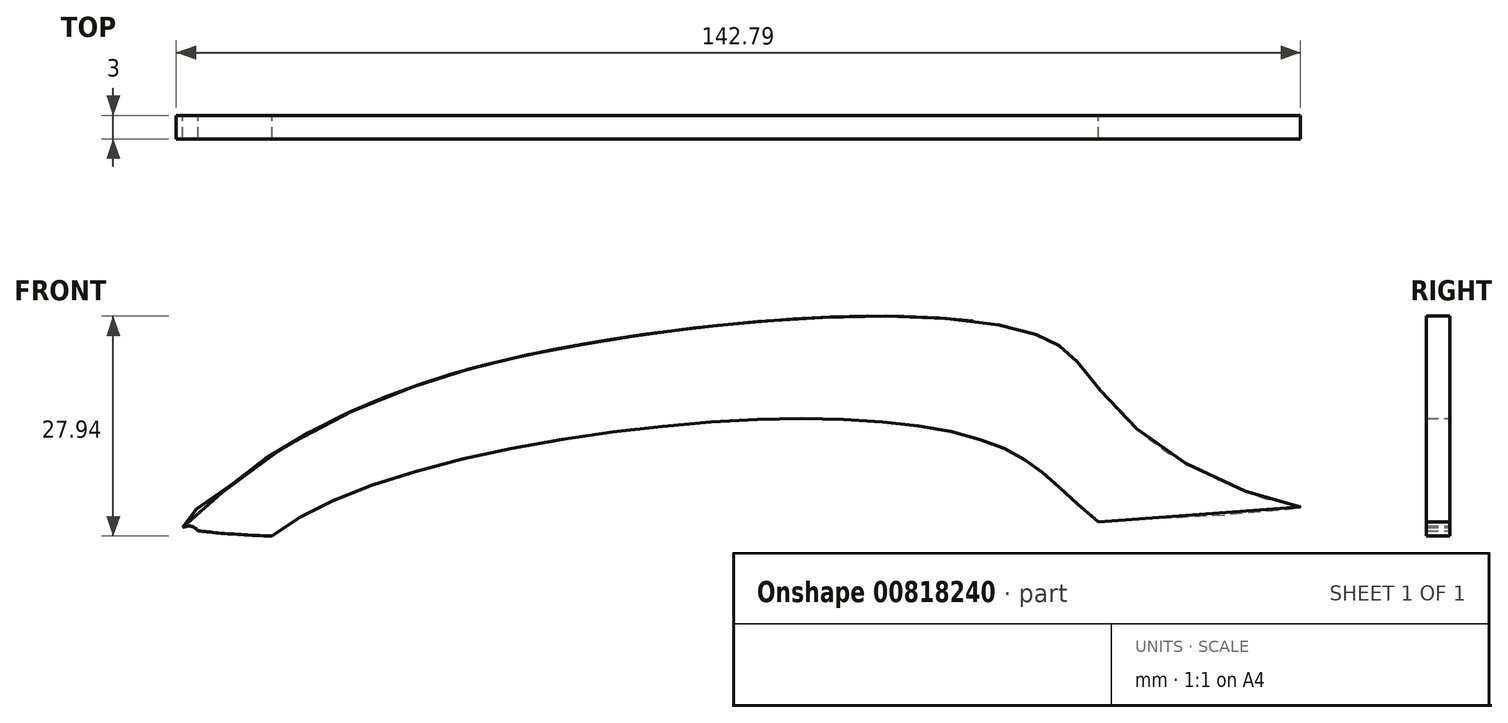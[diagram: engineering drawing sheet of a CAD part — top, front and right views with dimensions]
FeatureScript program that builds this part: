
annotation { "Feature Type Name" : "Feature", "Feature Type Description" : "" }
export const myFeature = defineFeature(function(context is Context, id is Id, definition is map)
    precondition{}
    {
        {
            var Q0;
            Q0=qCreatedBy(makeId("Front.planeOp"),FACE);
            var sketch = newSketch(context, id + "F0", { "sketchPlane" : qUnion([Q0])});
            skCircle(sketch, "E0", {"center": v(-68.28, 0) * mm, "radius": 1.5 * mm});
            skCircle(sketch, "E1", {"center": v(71.72, 0) * mm, "radius": 1.5 * mm});
            skArc(sketch, "E2", {"start": v(-73.43, 6.13) * mm, "mid": v(-73.34, -6.2) * mm, "end": v(-61.25, -3.82) * mm});
            skArc(sketch, "E3", {"start": v(67.99, -9.28) * mm, "mid": v(81.18, -3.23) * mm, "end": v(74.44, 9.62) * mm});
            skFitSpline(sketch, "E4", {"points": [v(-73.43, 6.13) * mm, v(-19, 30.54) * mm, v(44.44, 30.12) * mm, v(74.44, 9.62) * mm], "startDerivative": vector(148.64, 124.78) * mm, "endDerivative": vector(251.37, -71.25) * mm});
            skFitSpline(sketch, "E5", {"points": [v(-61.25, -3.82) * mm, v(-8.1, 14.18) * mm, v(36.46, 10.8) * mm, v(67.99, -9.28) * mm], "startDerivative": vector(43.16, 79.54) * mm, "endDerivative": vector(229.82, -92.38) * mm});
            skFitSpline(sketch, "E6.0", {"points": [v(-69.57, 1.53) * mm, v(-66.6, 4.03) * mm, v(-60.85, 8.45) * mm, v(-52.52, 13.63) * mm, v(-45.53, 17) * mm, v(-39.7, 19.23) * mm, v(-35.17, 20.71) * mm, v(-30.42, 22.03) * mm, v(-25.43, 23.2) * mm, v(-21.01, 24.09) * mm, v(-17.31, 24.75) * mm, v(-13.5, 25.38) * mm, v(-8.6, 26.1) * mm, v(-2.53, 26.85) * mm, v(3.58, 27.45) * mm, v(9.65, 27.88) * mm, v(15.57, 28.12) * mm, v(21.24, 28.15) * mm, v(26.55, 27.96) * mm, v(31.37, 27.53) * mm, v(34.89, 26.98) * mm, v(37.31, 26.42) * mm, v(38.92, 25.96) * mm, v(40.3, 25.46) * mm, v(41.22, 25.04) * mm, v(41.82, 24.71) * mm, v(42.37, 24.37) * mm, v(42.99, 23.93) * mm, v(43.69, 23.3) * mm, v(44.41, 22.57) * mm, v(45.19, 21.68) * mm, v(46.33, 20.28) * mm, v(48.03, 18.14) * mm, v(50.75, 15.16) * mm, v(54.38, 12.06) * mm, v(59.09, 9.08) * mm, v(65.05, 6.31) * mm, v(70.02, 4.64) * mm, v(72.8, 3.85) * mm, v(-69.57, 1.53) * mm]});
            skSolve(sketch);
        }
        {
            var Q0;
            Q0=makeQuery(id+"F0.imprint","IMPRINT",FACE,{"disambiguationData":[TD([[makeQuery(id+"F0.imprint","IMPRINT",EDGE,{"derivedFrom":sQuery(id+"F0.wireOp",EDGE,"E0")}),-1.0]])]});
            extrude(context, id + "F1", {"entities" : qUnion([Q0]), "depth" : 3 * mm, "offsetDistance" : 25 * mm});
        }
    });
